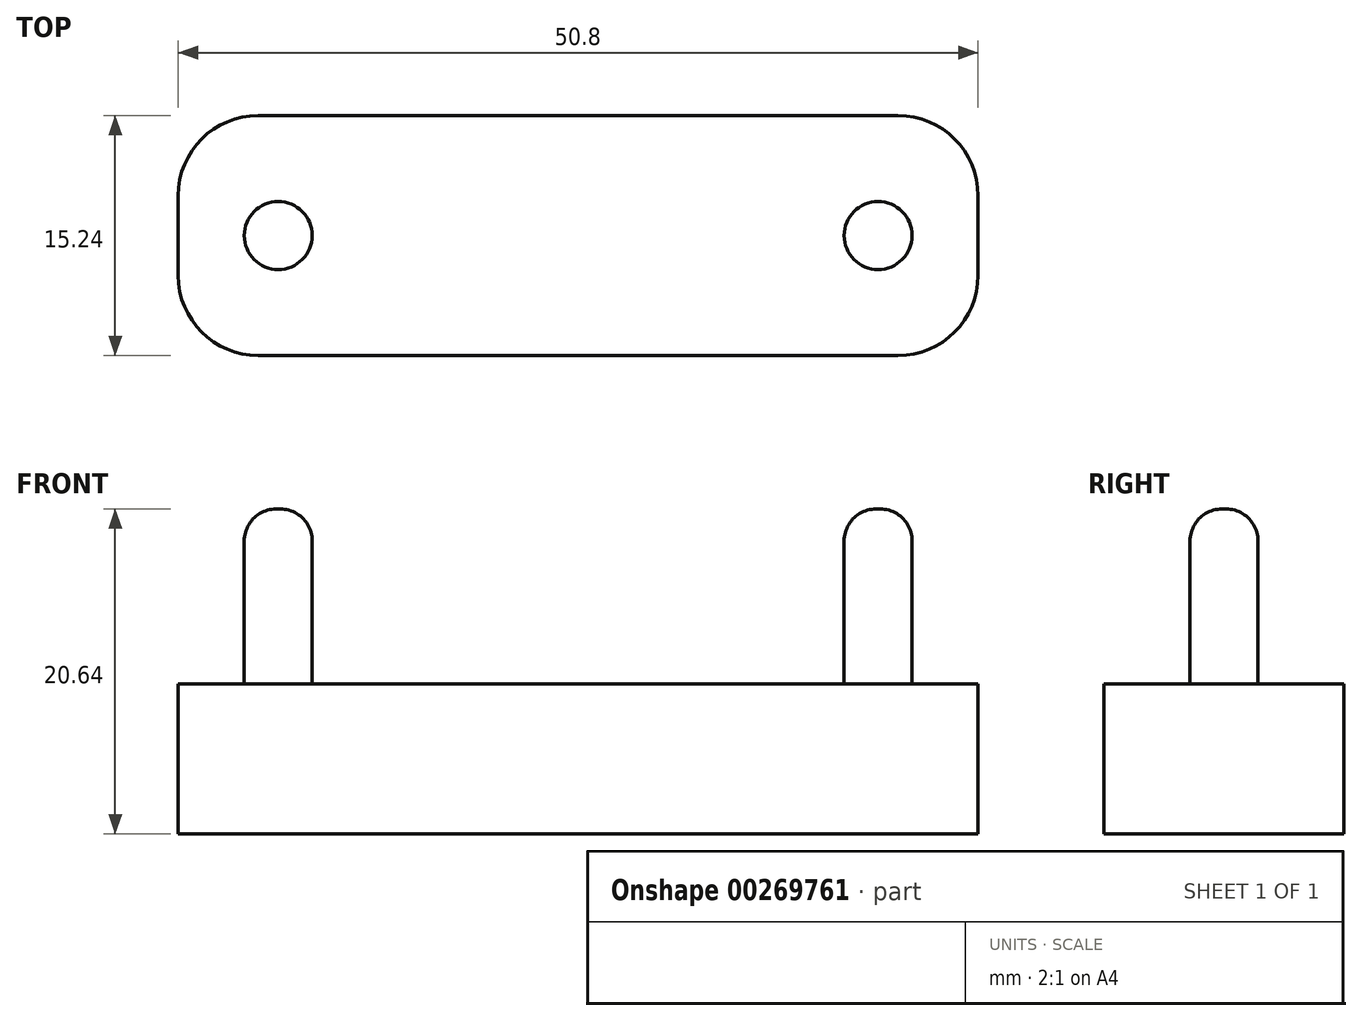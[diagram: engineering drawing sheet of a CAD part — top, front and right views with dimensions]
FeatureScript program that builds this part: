
annotation { "Feature Type Name" : "Feature", "Feature Type Description" : "" }
export const myFeature = defineFeature(function(context is Context, id is Id, definition is map)
    precondition{}
    {
        {
            var Q0;
            Q0=qCreatedBy(makeId("Top.planeOp"),FACE);
            var sketch = newSketch(context, id + "F0", { "sketchPlane" : qUnion([Q0])});
            skLineSegment(sketch, "E0.bottom", {"start": v(25.4, -7.62) * mm, "end": v(-25.4, -7.62) * mm});
            skLineSegment(sketch, "E0.top", {"start": v(25.4, 7.62) * mm, "end": v(-25.4, 7.62) * mm});
            skLineSegment(sketch, "E0.left", {"start": v(25.4, -7.62) * mm, "end": v(25.4, 7.62) * mm});
            skLineSegment(sketch, "E0.right", {"start": v(-25.4, -7.62) * mm, "end": v(-25.4, 7.62) * mm});
            skPoint(sketch, "E0.middle", {"position": v(0, 0) * mm});
            skSolve(sketch);
        }
        {
            var Q0;
            Q0=makeQuery(id+"F0.imprint","IMPRINT",FACE,{"disambiguationData":[TD([[makeQuery(id+"F0.imprint","IMPRINT",EDGE,{"derivedFrom":sQuery(id+"F0.wireOp",EDGE,"E0.bottom")}),-1.0]])]});
            extrude(context, id + "F1", {"entities" : qUnion([Q0]), "depth" : 9.52 * mm});
        }
        {
            var Q0;
            Q0=makeQuery(id+"F1.opExtrude","CAP_FACE",FACE,{"disambiguationData":[OSD([sQuery(id+"F0.wireOp",EDGE,"E0.bottom"),sQuery(id+"F0.wireOp",EDGE,"E0.top"),sQuery(id+"F0.wireOp",EDGE,"E0.left"),sQuery(id+"F0.wireOp",EDGE,"E0.right")])],"isStart":false});
            var sketch = newSketch(context, id + "F2", { "sketchPlane" : qUnion([Q0])});
            skCircle(sketch, "E1", {"center": v(19.05, 0) * mm, "radius": 2.16 * mm});
            skCircle(sketch, "E2", {"center": v(-19.05, 0) * mm, "radius": 2.16 * mm});
            skSolve(sketch);
        }
        {
            var Q0;
            Q0=makeQuery(id+"F2.imprint","IMPRINT",FACE,{"disambiguationData":[TD([[makeQuery(id+"F2.imprint","IMPRINT",EDGE,{"derivedFrom":sQuery(id+"F2.wireOp",EDGE,"E2")}),1.0]])]});
            var Q1;
            Q1=makeQuery(id+"F2.imprint","IMPRINT",FACE,{"disambiguationData":[TD([[makeQuery(id+"F2.imprint","IMPRINT",EDGE,{"derivedFrom":sQuery(id+"F2.wireOp",EDGE,"E1")}),1.0]])]});
            extrude(context, id + "F3", {"entities" : qUnion([Q0, Q1]), "operationType" : NewBodyOperationType.ADD, "depth" : 11.1 * mm});
        }
        {
            var Q0;
            Q0=makeQuery(id+"F3.opExtrude","CAP_EDGE",EDGE,{"disambiguationData":[OSD([sQuery(id+"F2.wireOp",EDGE,"E2")])],"isStart":false});
            var Q1;
            Q1=makeQuery(id+"F3.opExtrude","CAP_EDGE",EDGE,{"disambiguationData":[OSD([sQuery(id+"F2.wireOp",EDGE,"E1")])],"isStart":false});
            fillet(context, id + "F4", {"entities" : qUnion([Q0, Q1]), "radius" : 2.03 * mm, "tangentPropagation" : true, "allowEdgeOverflow" : false});
        }
        {
            var Q0;
            Q0=makeQuery(id+"F1.opExtrude","SWEPT_EDGE",EDGE,{"disambiguationData":[OSD([sQuery(id+"F0.wireOp",EDGE,"E0.bottom"),sQuery(id+"F0.wireOp",EDGE,"E0.right")])]});
            var Q1;
            Q1=makeQuery(id+"F1.opExtrude","SWEPT_EDGE",EDGE,{"disambiguationData":[OSD([sQuery(id+"F0.wireOp",EDGE,"E0.bottom"),sQuery(id+"F0.wireOp",EDGE,"E0.left")])]});
            var Q2;
            Q2=makeQuery(id+"F1.opExtrude","SWEPT_EDGE",EDGE,{"disambiguationData":[OSD([sQuery(id+"F0.wireOp",EDGE,"E0.top"),sQuery(id+"F0.wireOp",EDGE,"E0.left")])]});
            var Q3;
            Q3=makeQuery(id+"F1.opExtrude","SWEPT_EDGE",EDGE,{"disambiguationData":[OSD([sQuery(id+"F0.wireOp",EDGE,"E0.top"),sQuery(id+"F0.wireOp",EDGE,"E0.right")])]});
            fillet(context, id + "F5", {"entities" : qUnion([Q0, Q1, Q2, Q3]), "radius" : 5.08 * mm, "tangentPropagation" : true, "allowEdgeOverflow" : false});
        }
    });
